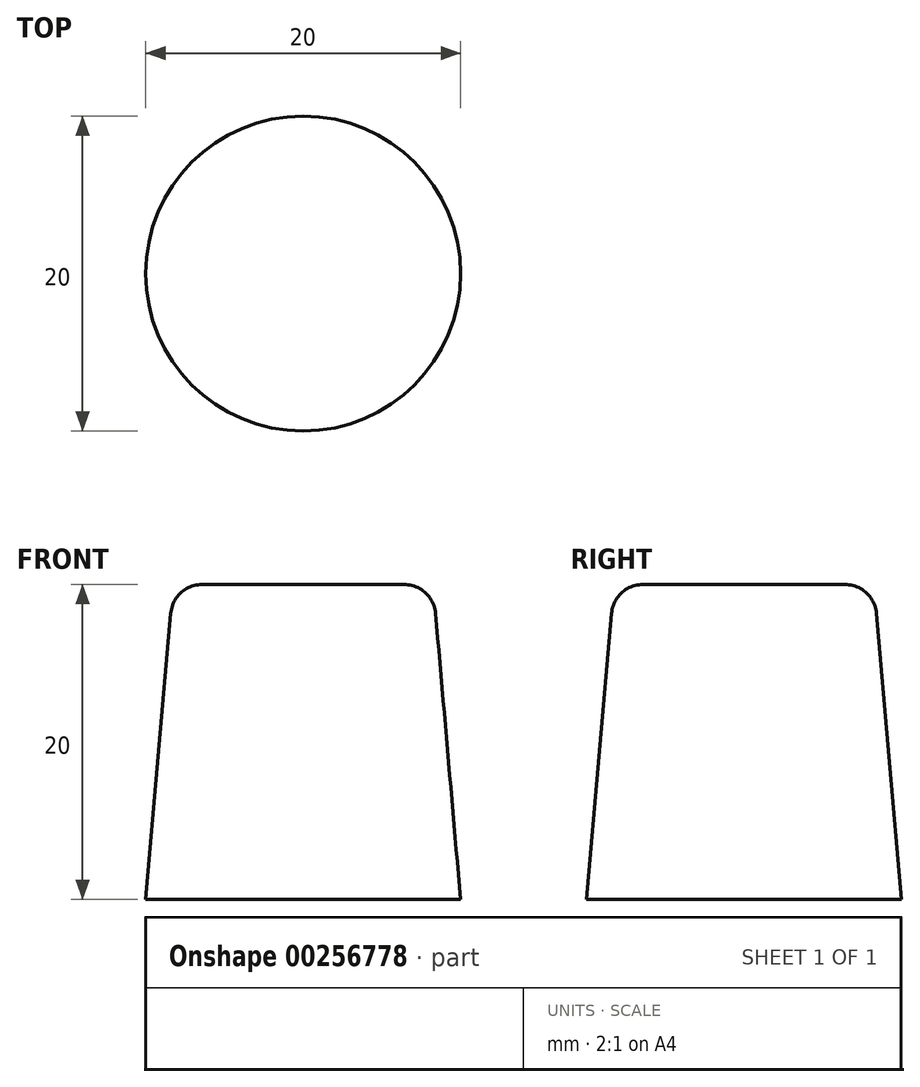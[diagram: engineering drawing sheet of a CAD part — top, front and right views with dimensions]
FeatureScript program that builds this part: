
annotation { "Feature Type Name" : "Feature", "Feature Type Description" : "" }
export const myFeature = defineFeature(function(context is Context, id is Id, definition is map)
    precondition{}
    {
        {
            var Q0;
            Q0=qCreatedBy(makeId("Top.planeOp"),FACE);
            var sketch = newSketch(context, id + "F0", { "sketchPlane" : qUnion([Q0])});
            skCircle(sketch, "E0", {"center": v(0, 0) * mm, "radius": 10 * mm});
            skSolve(sketch);
        }
        {
            var Q0;
            Q0 = qSketchRegion(id + "F0", true);
            extrude(context, id + "F1", {"entities" : qUnion([Q0]), "depth" : 20 * mm, "hasDraft" : true, "draftAngle" : 5 * degree, "draftPullDirection" : true});
        }
        {
            var Q0;
            Q0=makeQuery(id+"F1.opExtrude","CAP_EDGE",EDGE,{"disambiguationData":[OSD([sQuery(id+"F0.wireOp",EDGE,"E0")])],"isStart":false});
            fillet(context, id + "F2", {"entities" : qUnion([Q0]), "radius" : 2 * mm, "tangentPropagation" : true, "allowEdgeOverflow" : false});
        }
    });
